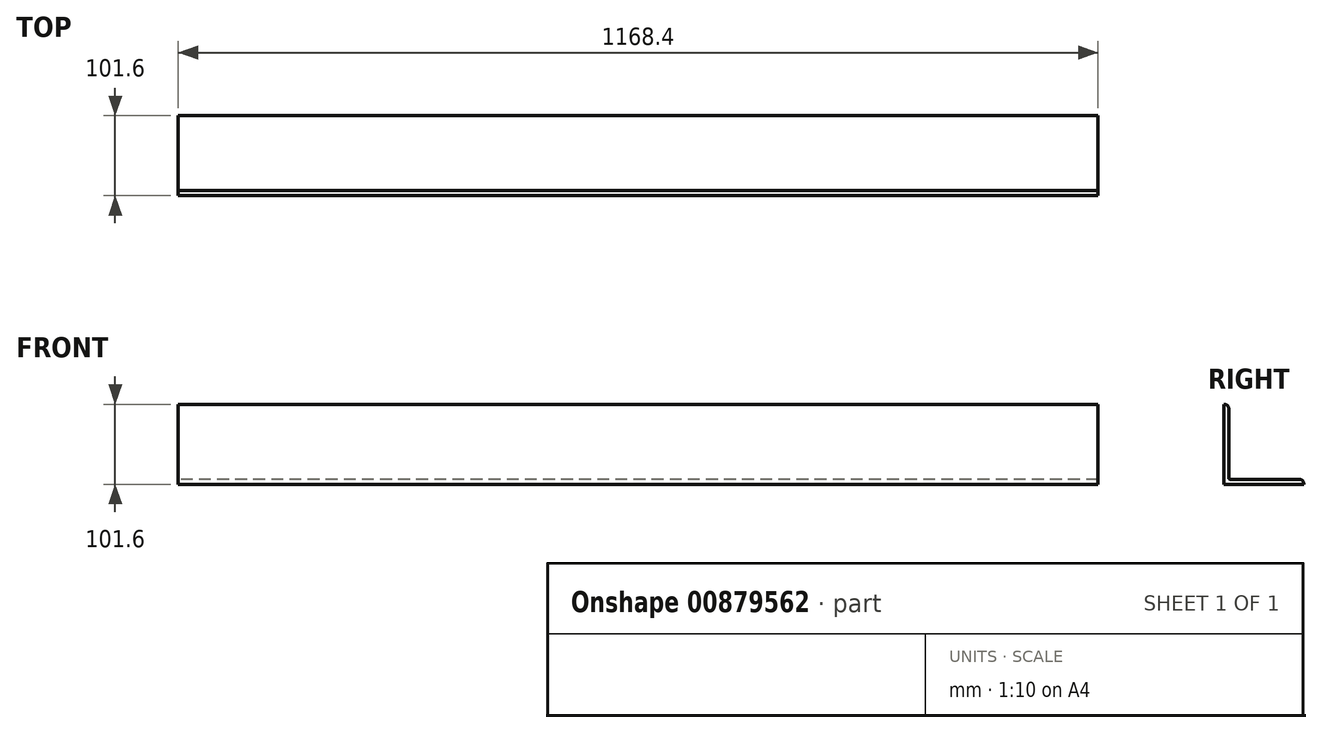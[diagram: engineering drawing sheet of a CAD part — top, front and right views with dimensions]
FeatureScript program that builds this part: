
annotation { "Feature Type Name" : "Feature", "Feature Type Description" : "" }
export const myFeature = defineFeature(function(context is Context, id is Id, definition is map)
    precondition{}
    {
        {
            var Q0;
            Q0=qCreatedBy(makeId("Right.planeOp"),FACE);
            var sketch = newSketch(context, id + "F0", { "sketchPlane" : qUnion([Q0])});
            skLineSegment(sketch, "E0", {"start": v(0, 0) * mm, "end": v(101.6, 0) * mm});
            skLineSegment(sketch, "E1", {"start": v(0, 0) * mm, "end": v(0, 101.6) * mm});
            skLineSegment(sketch, "E2.0", {"start": v(6.35, 7.62) * mm, "end": v(6.35, 95.25) * mm});
            skLineSegment(sketch, "E2.1", {"start": v(7.62, 6.35) * mm, "end": v(95.25, 6.35) * mm});
            skLineSegment(sketch, "E3", {"start": v(0, 101.6) * mm, "end": v(0, 101.6) * mm});
            skArc(sketch, "E4.filletArc", {"start": v(6.35, 95.25) * mm, "mid": v(4.5, 99.74) * mm, "end": v(0, 101.6) * mm});
            skLineSegment(sketch, "E5", {"start": v(101.6, 0) * mm, "end": v(101.6, 0) * mm});
            skArc(sketch, "E6.filletArc", {"start": v(101.6, 0) * mm, "mid": v(99.74, 4.5) * mm, "end": v(95.25, 6.35) * mm});
            skPoint(sketch, "E7.visualSharp", {"position": v(6.35, 6.35) * mm});
            skArc(sketch, "E7.filletArc", {"start": v(6.35, 7.62) * mm, "mid": v(6.72, 6.72) * mm, "end": v(7.62, 6.35) * mm});
            skSolve(sketch);
        }
        {
            var Q0;
            Q0=makeQuery(id+"F0.imprint","IMPRINT",FACE,{"disambiguationData":[TD([[makeQuery(id+"F0.imprint","IMPRINT",EDGE,{"derivedFrom":sQuery(id+"F0.wireOp",EDGE,"E0")}),1.0]])]});
            extrude(context, id + "F1", {"entities" : qUnion([Q0]), "depth" : 1168.4 * mm, "offsetDistance" : 25.4 * mm});
        }
    });
